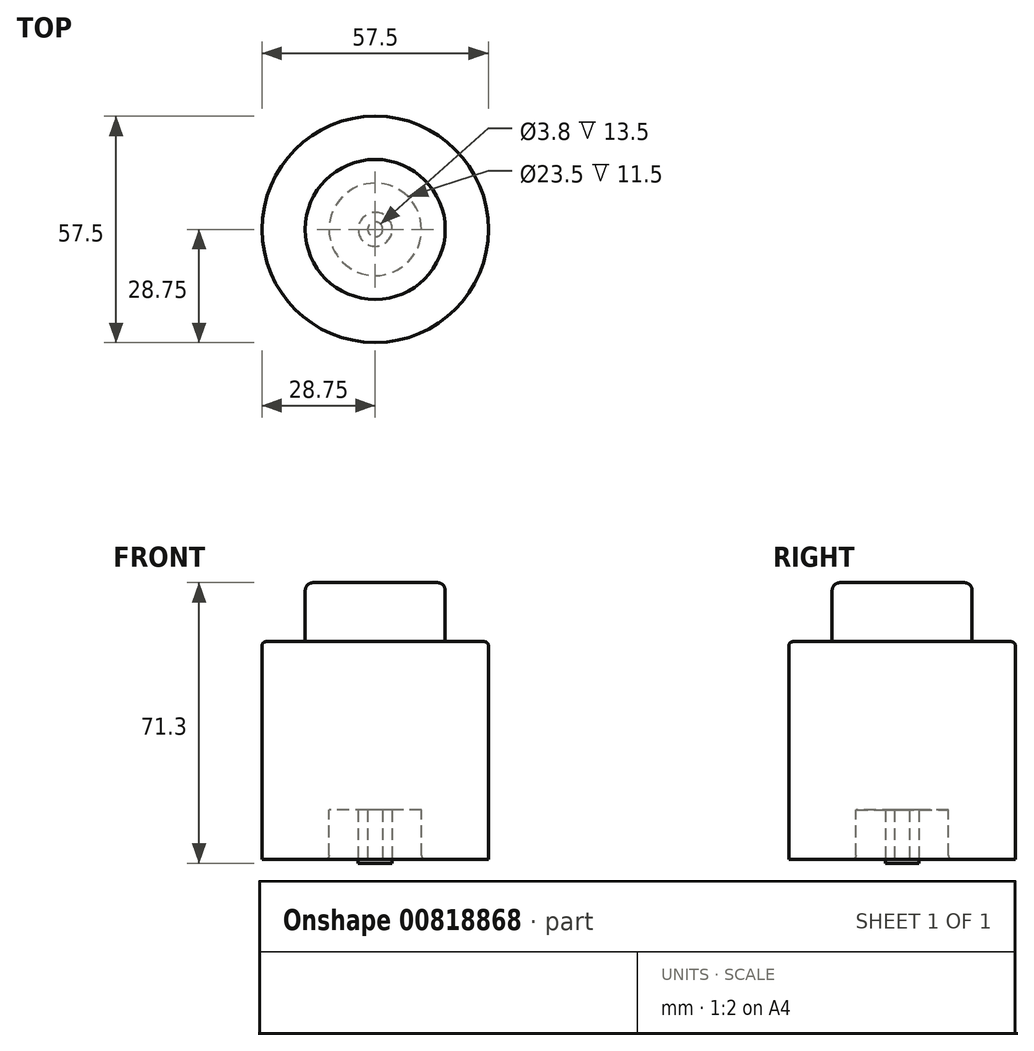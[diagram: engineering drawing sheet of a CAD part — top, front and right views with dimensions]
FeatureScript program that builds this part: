
annotation { "Feature Type Name" : "Feature", "Feature Type Description" : "" }
export const myFeature = defineFeature(function(context is Context, id is Id, definition is map)
    precondition{}
    {
        {
            var Q0;
            Q0=qCreatedBy(makeId("Top.planeOp"),FACE);
            var sketch = newSketch(context, id + "F0", { "sketchPlane" : qUnion([Q0])});
            skCircle(sketch, "E0", {"center": v(0, 0) * mm, "radius": 4.3 * mm});
            skCircle(sketch, "E1", {"center": v(0, 0) * mm, "radius": 1.9 * mm});
            skSolve(sketch);
        }
        {
            var Q0;
            Q0 = qSketchRegion(id + "F0", true);
            extrude(context, id + "F1", {"entities" : qUnion([Q0]), "depth" : 13.5 * mm, "offsetDistance" : 25 * mm});
        }
        {
            var Q0;
            Q0=makeQuery(id+"F1.opExtrude","CAP_FACE",FACE,{"disambiguationData":[OSD([sQuery(id+"F0.wireOp",EDGE,"E0"),sQuery(id+"F0.wireOp",EDGE,"E1")])],"isStart":false});
            var sketch = newSketch(context, id + "F2", { "sketchPlane" : qUnion([Q0])});
            skCircle(sketch, "E2", {"center": v(0, 0) * mm, "radius": 28.75 * mm});
            skCircle(sketch, "E3", {"center": v(0, 0) * mm, "radius": 11.75 * mm});
            skSolve(sketch);
        }
        {
            var Q0;
            Q0 = qSketchRegion(id + "F2", true);
            extrude(context, id + "F3", {"entities" : qUnion([Q0]), "oppositeDirection" : true, "depth" : 12.5 * mm, "offsetDistance" : 25 * mm});
        }
        {
            var Q0;
            Q0=makeQuery(id+"F1.opExtrude","CAP_FACE",FACE,{"disambiguationData":[OSD([sQuery(id+"F0.wireOp",EDGE,"E0"),sQuery(id+"F0.wireOp",EDGE,"E1")])],"isStart":false});
            var sketch = newSketch(context, id + "F4", { "sketchPlane" : qUnion([Q0])});
            skCircle(sketch, "E4", {"center": v(0, 0) * mm, "radius": 28.75 * mm});
            skSolve(sketch);
        }
        {
            var Q0;
            Q0 = qSketchRegion(id + "F4", true);
            extrude(context, id + "F5", {"entities" : qUnion([Q0]), "operationType" : NewBodyOperationType.ADD, "depth" : (2 * 25.4 - 8) * mm, "offsetDistance" : 25 * mm});
        }
        {
            var Q0;
            Q0=makeQuery(id+"F5.opExtrude","CAP_FACE",FACE,{"disambiguationData":[OSD([sQuery(id+"F4.wireOp",EDGE,"E4")])],"isStart":false});
            var sketch = newSketch(context, id + "F6", { "sketchPlane" : qUnion([Q0])});
            skCircle(sketch, "E5", {"center": v(0, 0) * mm, "radius": 17.78 * mm});
            skSolve(sketch);
        }
        {
            var Q0;
            Q0 = qSketchRegion(id + "F6", true);
            extrude(context, id + "F7", {"entities" : qUnion([Q0]), "operationType" : NewBodyOperationType.ADD, "flatOperationType" : FlatOperationType.REMOVE, "depth" : 15 * mm, "offsetDistance" : 25 * mm, "domain" : OperationDomain.MODEL});
        }
        {
            var Q0;
            Q0=makeQuery(id+"F7.opExtrude","CAP_EDGE",EDGE,{"disambiguationData":[OSD([sQuery(id+"F6.wireOp",EDGE,"E5")])],"isStart":false});
            fillet(context, id + "F8", {"entities" : qUnion([Q0]), "radius" : 2 * mm, "tangentPropagation" : true, "allowEdgeOverflow" : false});
        }
        {
            var Q0;
            Q0=makeQuery(id+"F5.opExtrude","CAP_EDGE",EDGE,{"disambiguationData":[OSD([sQuery(id+"F4.wireOp",EDGE,"E4")])],"isStart":false});
            fillet(context, id + "F9", {"entities" : qUnion([Q0]), "radius" : 1 * mm, "tangentPropagation" : true, "allowEdgeOverflow" : false});
        }
        {
            var Q0;
            Q0=makeQuery(id+"F3.opExtrude","CAP_EDGE",EDGE,{"disambiguationData":[OSD([sQuery(id+"F2.wireOp",EDGE,"E3")])],"isStart":false});
            fillet(context, id + "F10", {"entities" : qUnion([Q0]), "radius" : 1 * mm, "tangentPropagation" : true, "allowEdgeOverflow" : false});
        }
    });
